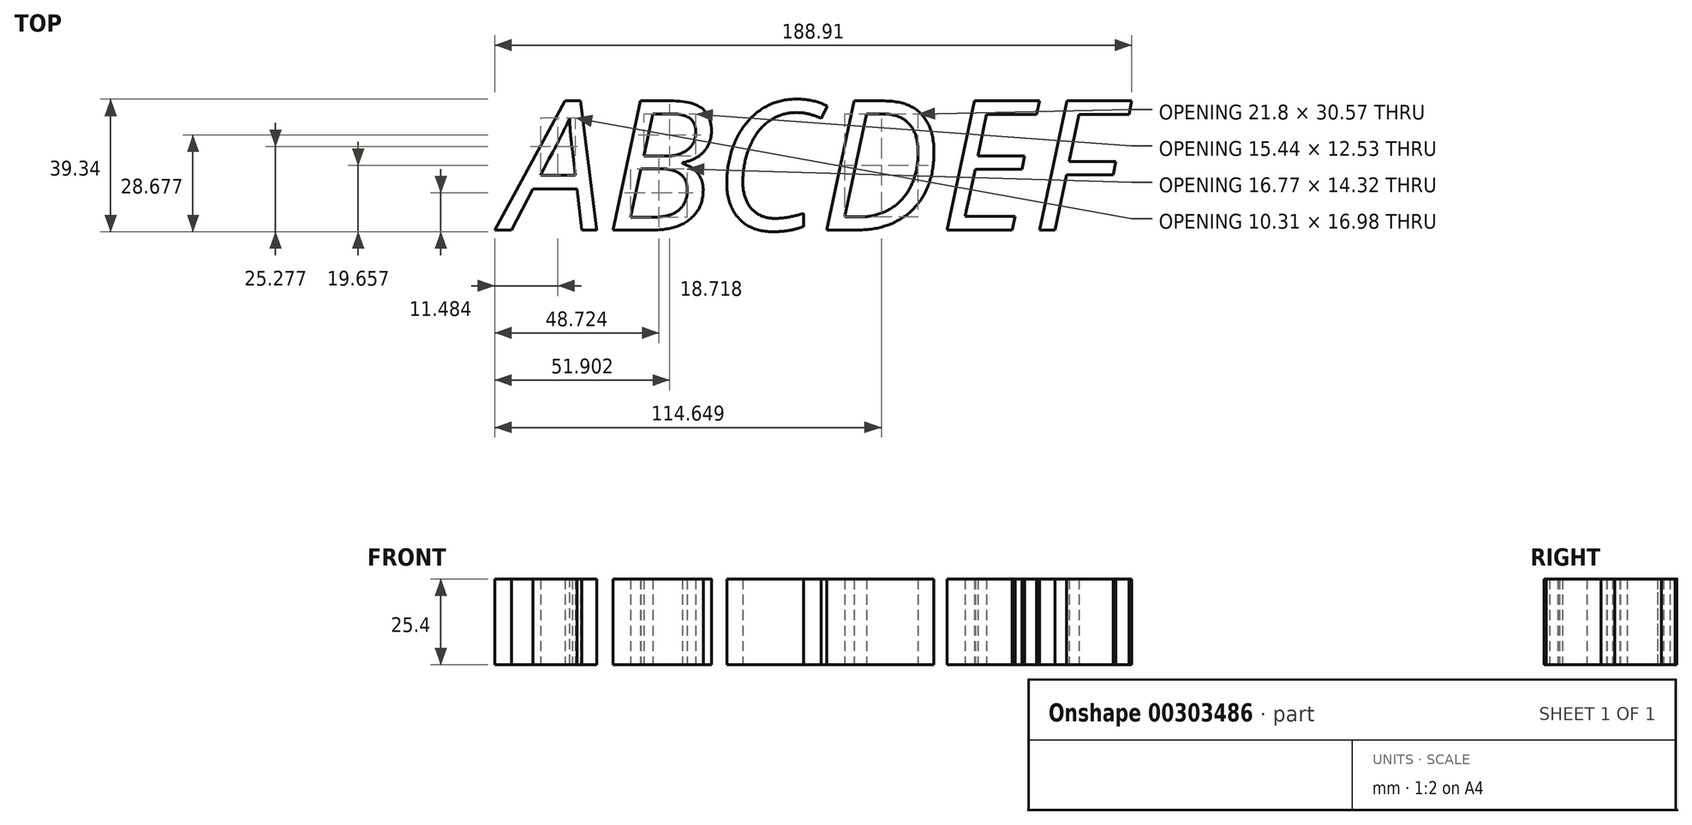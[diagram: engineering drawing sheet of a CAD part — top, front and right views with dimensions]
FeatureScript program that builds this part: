
annotation { "Feature Type Name" : "Feature", "Feature Type Description" : "" }
export const myFeature = defineFeature(function(context is Context, id is Id, definition is map)
    precondition{}
    {
        {
            var Q0;
            Q0=qCreatedBy(makeId("Top.planeOp"),FACE);
            var sketch = newSketch(context, id + "F0", { "sketchPlane" : qUnion([Q0])});
            skText(sketch, "E0", { "text": "ABCDEFG", "fontName": "OpenSans-Italic.ttf"});
            const initialGuessF0  = {"E0": [-0.13145, -0.02804, 1, 0, 0.03859]};
            skSetInitialGuess(sketch, initialGuessF0);
            skSolve(sketch);
        }
        {
            var Q0;
            Q0 = qSketchRegion(id + "F0", true);
            extrude(context, id + "F1", {"entities" : qUnion([Q0]), "depth" : 25.4 * mm});
        }
        {
            var Q0;
            Q0=makeQuery(id+"F1.opExtrude","SWEPT_BODY",BODY,{"disambiguationData":[OSD([sQuery(id+"F0.wireOp",EDGE,"E0.sketch_text.stroke-93"),sQuery(id+"F0.wireOp",EDGE,"E0.sketch_text.stroke-94"),sQuery(id+"F0.wireOp",EDGE,"E0.sketch_text.stroke-95"),sQuery(id+"F0.wireOp",EDGE,"E0.sketch_text.stroke-96"),sQuery(id+"F0.wireOp",EDGE,"E0.sketch_text.stroke-97"),sQuery(id+"F0.wireOp",EDGE,"E0.sketch_text.stroke-98"),sQuery(id+"F0.wireOp",EDGE,"E0.sketch_text.stroke-99"),sQuery(id+"F0.wireOp",EDGE,"E0.sketch_text.stroke-100"),sQuery(id+"F0.wireOp",EDGE,"E0.sketch_text.stroke-101"),sQuery(id+"F0.wireOp",EDGE,"E0.sketch_text.stroke-102"),sQuery(id+"F0.wireOp",EDGE,"E0.sketch_text.stroke-103"),sQuery(id+"F0.wireOp",EDGE,"E0.sketch_text.stroke-104"),sQuery(id+"F0.wireOp",EDGE,"E0.sketch_text.stroke-105"),sQuery(id+"F0.wireOp",EDGE,"E0.sketch_text.stroke-106"),sQuery(id+"F0.wireOp",EDGE,"E0.sketch_text.stroke-107"),sQuery(id+"F0.wireOp",EDGE,"E0.sketch_text.stroke-108"),sQuery(id+"F0.wireOp",EDGE,"E0.sketch_text.stroke-109"),sQuery(id+"F0.wireOp",EDGE,"E0.sketch_text.stroke-110"),sQuery(id+"F0.wireOp",EDGE,"E0.sketch_text.stroke-111"),sQuery(id+"F0.wireOp",EDGE,"E0.sketch_text.stroke-112"),sQuery(id+"F0.wireOp",EDGE,"E0.sketch_text.stroke-113"),sQuery(id+"F0.wireOp",EDGE,"E0.sketch_text.stroke-114")])]});
            deleteBodies(context, id + "F2", {"entities" : qUnion([Q0])});
        }
    });
